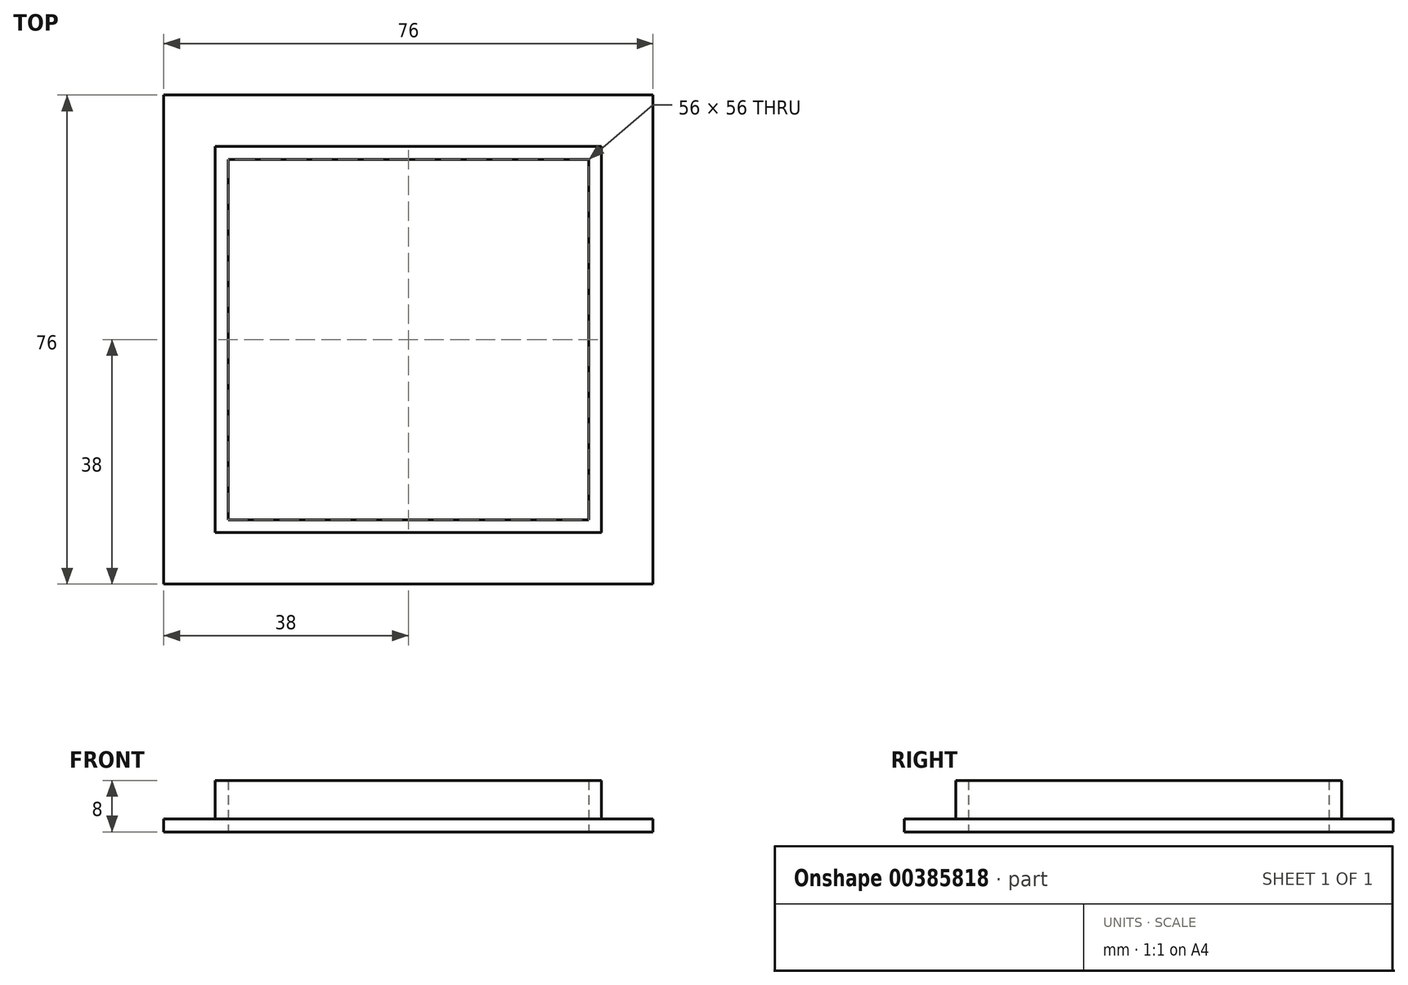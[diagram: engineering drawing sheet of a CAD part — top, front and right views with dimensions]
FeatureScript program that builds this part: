
annotation { "Feature Type Name" : "Feature", "Feature Type Description" : "" }
export const myFeature = defineFeature(function(context is Context, id is Id, definition is map)
    precondition{}
    {
        {
            var Q0;
            Q0=qCreatedBy(makeId("Top.planeOp"),FACE);
            var sketch = newSketch(context, id + "F0", { "sketchPlane" : qUnion([Q0])});
            skLineSegment(sketch, "E0.bottom", {"start": v(0, 0) * mm, "end": v(56, 0) * mm});
            skLineSegment(sketch, "E0.top", {"start": v(0, 56) * mm, "end": v(56, 56) * mm});
            skLineSegment(sketch, "E0.left", {"start": v(0, 0) * mm, "end": v(0, 56) * mm});
            skLineSegment(sketch, "E0.right", {"start": v(56, 0) * mm, "end": v(56, 56) * mm});
            skLineSegment(sketch, "E1.0", {"start": v(66, -10) * mm, "end": v(66, 66) * mm});
            skLineSegment(sketch, "E1.1", {"start": v(-10, -10) * mm, "end": v(66, -10) * mm});
            skLineSegment(sketch, "E1.2", {"start": v(-10, -10) * mm, "end": v(-10, 66) * mm});
            skLineSegment(sketch, "E1.3", {"start": v(-10, 66) * mm, "end": v(66, 66) * mm});
            skSolve(sketch);
        }
        {
            var Q0;
            Q0 = qSketchRegion(id + "F0", true);
            extrude(context, id + "F1", {"entities" : qUnion([Q0]), "depth" : 2 * mm});
        }
        {
            var Q0;
            Q0=makeQuery(id+"F1.opExtrude","CAP_FACE",FACE,{"disambiguationData":[OSD([sQuery(id+"F0.wireOp",EDGE,"E0.bottom"),sQuery(id+"F0.wireOp",EDGE,"E0.top"),sQuery(id+"F0.wireOp",EDGE,"E0.left"),sQuery(id+"F0.wireOp",EDGE,"E0.right"),sQuery(id+"F0.wireOp",EDGE,"E1.0"),sQuery(id+"F0.wireOp",EDGE,"E1.1"),sQuery(id+"F0.wireOp",EDGE,"E1.2"),sQuery(id+"F0.wireOp",EDGE,"E1.3")])],"isStart":false});
            var sketch = newSketch(context, id + "F2", { "sketchPlane" : qUnion([Q0])});
            skLineSegment(sketch, "E2.0", {"start": v(0, 56) * mm, "end": v(56, 56) * mm});
            skLineSegment(sketch, "E2.1", {"start": v(0, 0) * mm, "end": v(0, 56) * mm});
            skLineSegment(sketch, "E2.2", {"start": v(0, 0) * mm, "end": v(56, 0) * mm});
            skLineSegment(sketch, "E2.3", {"start": v(56, 0) * mm, "end": v(56, 56) * mm});
            skLineSegment(sketch, "E3.0", {"start": v(-2, 58) * mm, "end": v(58, 58) * mm});
            skLineSegment(sketch, "E3.1", {"start": v(-2, -2) * mm, "end": v(-2, 58) * mm});
            skLineSegment(sketch, "E3.2", {"start": v(-2, -2) * mm, "end": v(58, -2) * mm});
            skLineSegment(sketch, "E3.3", {"start": v(58, -2) * mm, "end": v(58, 58) * mm});
            skSolve(sketch);
        }
        {
            var Q0;
            Q0 = qSketchRegion(id + "F2", true);
            extrude(context, id + "F3", {"entities" : qUnion([Q0]), "operationType" : NewBodyOperationType.ADD, "depth" : 6 * mm});
        }
    });
